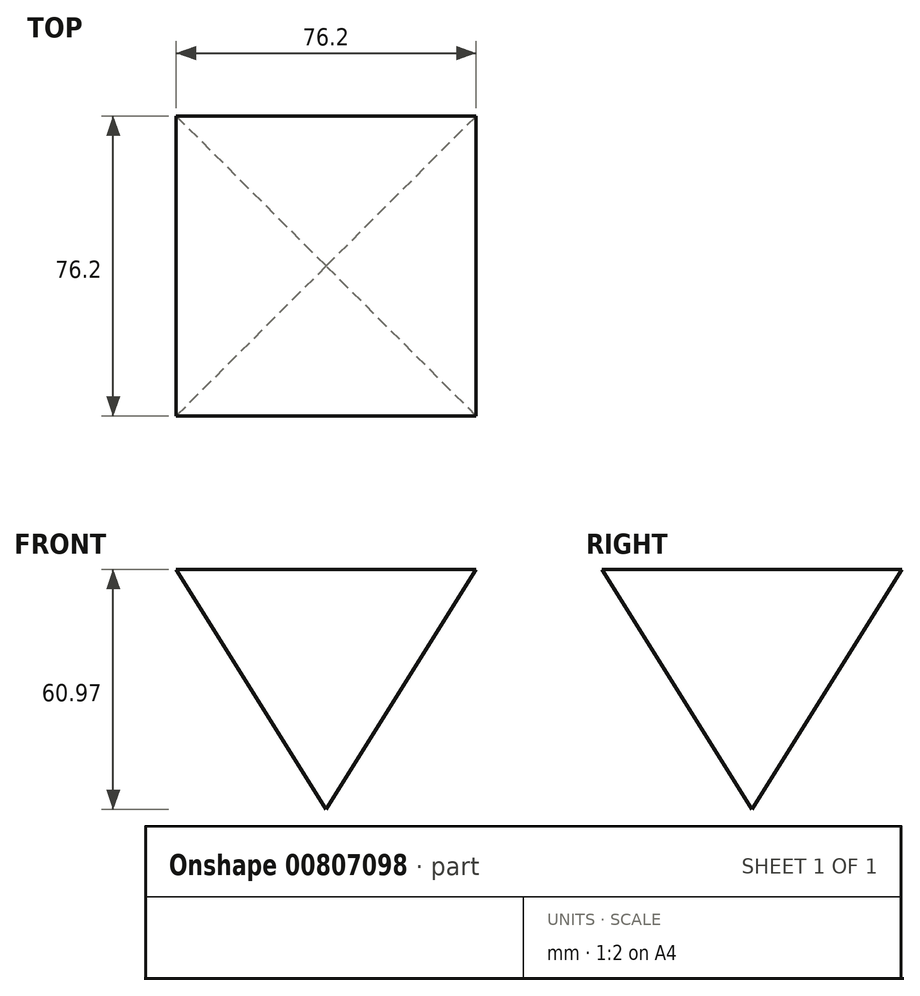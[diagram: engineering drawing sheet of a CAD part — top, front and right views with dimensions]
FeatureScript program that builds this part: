
annotation { "Feature Type Name" : "Feature", "Feature Type Description" : "" }
export const myFeature = defineFeature(function(context is Context, id is Id, definition is map)
    precondition{}
    {
        {
            var Q0;
            Q0=qCreatedBy(makeId("Top.planeOp"),FACE);
            var sketch = newSketch(context, id + "F0", { "sketchPlane" : qUnion([Q0])});
            skLineSegment(sketch, "E0.bottom", {"start": v(-11.03, 19.92) * mm, "end": v(65.17, 19.92) * mm});
            skLineSegment(sketch, "E0.top", {"start": v(-11.03, -56.28) * mm, "end": v(65.17, -56.28) * mm});
            skLineSegment(sketch, "E0.left", {"start": v(-11.03, 19.92) * mm, "end": v(-11.03, -56.28) * mm});
            skLineSegment(sketch, "E0.right", {"start": v(65.17, 19.92) * mm, "end": v(65.17, -56.28) * mm});
            skSolve(sketch);
        }
        {
            var Q0;
            Q0=makeQuery(id+"F0.imprint","IMPRINT",FACE,{"disambiguationData":[TD([[makeQuery(id+"F0.imprint","IMPRINT",EDGE,{"derivedFrom":sQuery(id+"F0.wireOp",EDGE,"E0.bottom")}),-1.0]])]});
            extrude(context, id + "F1", {"entities" : qUnion([Q0]), "oppositeDirection" : true, "depth" : 112.52 * mm, "offsetDistance" : 25.4 * mm, "hasDraft" : true, "draftAngle" : 32 * degree, "draftPullDirection" : true});
        }
    });
